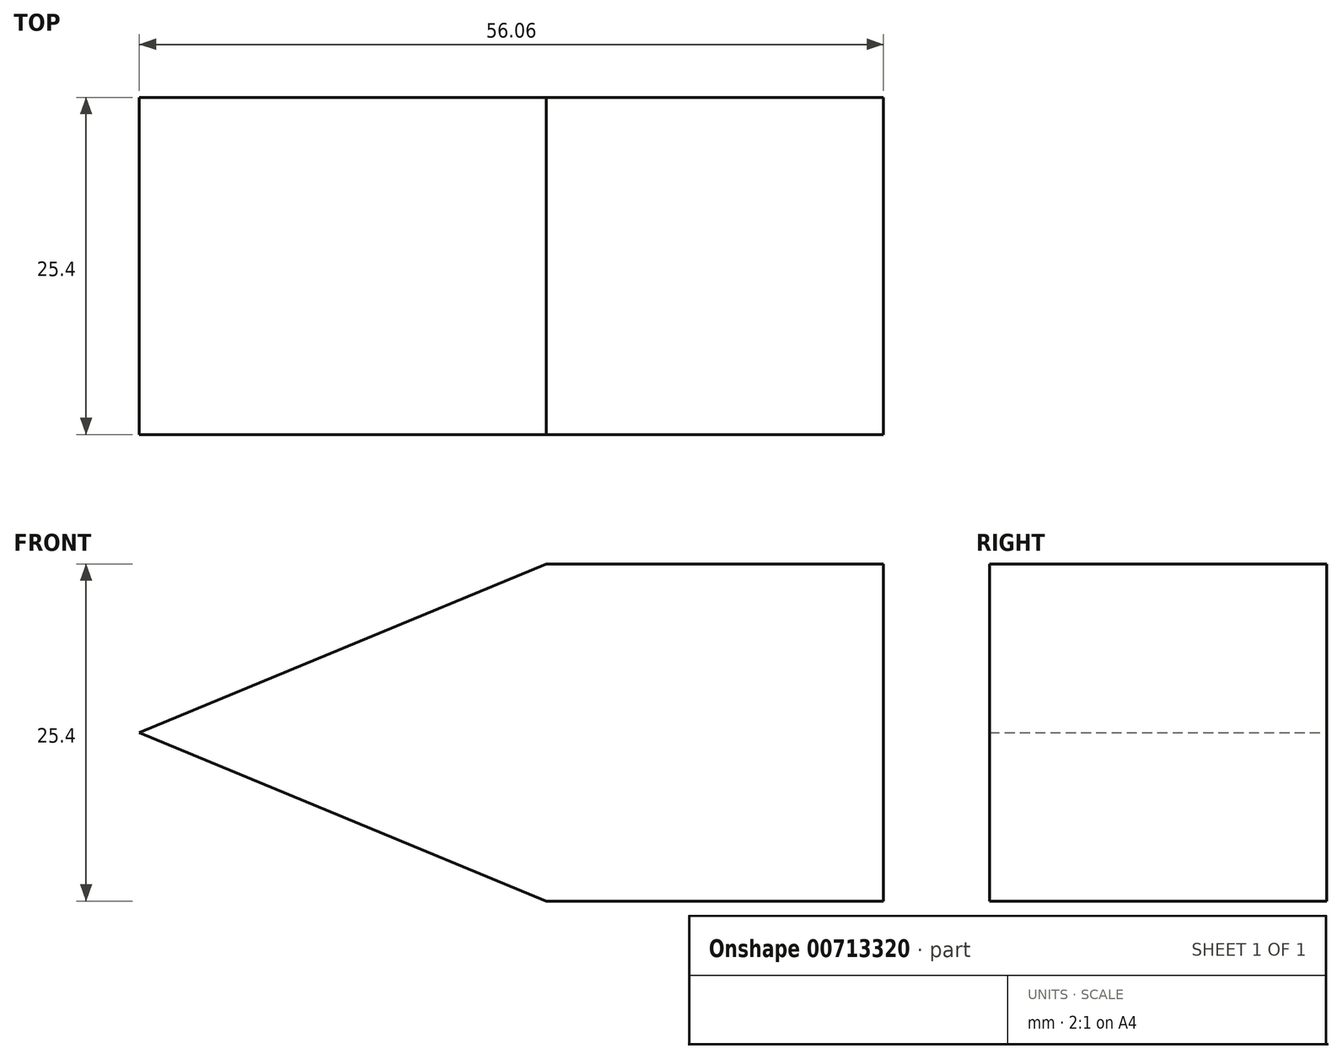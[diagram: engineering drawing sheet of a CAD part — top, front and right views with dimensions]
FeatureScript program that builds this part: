
annotation { "Feature Type Name" : "Feature", "Feature Type Description" : "" }
export const myFeature = defineFeature(function(context is Context, id is Id, definition is map)
    precondition{}
    {
        {
            var Q0;
            Q0=qCreatedBy(makeId("Front.planeOp"),FACE);
            var sketch = newSketch(context, id + "F0", { "sketchPlane" : qUnion([Q0])});
            skLineSegment(sketch, "E0.bottom", {"start": v(0, 0) * mm, "end": v(25.4, 0) * mm});
            skLineSegment(sketch, "E0.top", {"start": v(0, -25.4) * mm, "end": v(25.4, -25.4) * mm});
            skLineSegment(sketch, "E0.right", {"start": v(25.4, 0) * mm, "end": v(25.4, -25.4) * mm});
            skLineSegment(sketch, "E1", {"start": v(0, 0) * mm, "end": v(-30.66, -12.7) * mm});
            skLineSegment(sketch, "E2", {"start": v(-30.66, -12.7) * mm, "end": v(0, -25.4) * mm});
            skSolve(sketch);
        }
        {
            var Q0;
            Q0=makeQuery(id+"F0.imprint","IMPRINT",FACE,{"disambiguationData":[TD([[makeQuery(id+"F0.imprint","IMPRINT",EDGE,{"derivedFrom":sQuery(id+"F0.wireOp",EDGE,"E0.bottom")}),-1.0]])]});
            extrude(context, id + "F1", {"entities" : qUnion([Q0]), "depth" : 25.4 * mm, "offsetDistance" : 25.4 * mm});
        }
    });
